# Revit family: ledwall-mounted-p_rd300-15w_543011000600
name_source: partatom
category: Leuchten
revit_build: Autodesk Revit 2016 (Build: 20190508_0715(x64)
units: mm (PartAtom-declared; Revit-internal decimal feet)

## family parameters
Basisbauteil = Fläche
Beim Laden mit Abzugskörper schneiden = Nein
Bemaßung runder Anschluss = Durchmesser verwenden
Gemeinsam genutzt = Nein
Lichtquelle = Nein
Raumberechnungspunkt = Nein
Teiletyp = Normal

## types (1)
- LEDWall-Mounted-P Rd300-15W (1 x LED, 1750 lm)
    Approval mark = CE, ENEC
    Beschreibung = Robust, waterproof IP65 LED luminaire with high degree impact protection (IK10). Well integrated in architecture thanks to its comfortable light distribution. Designed to be easy to install and maintain with up to 2.5mm² through-wiring possibility. Suitable for both indoor and outdoor applications. Energy savings up to 60% compared to compact fluorescent based fixtures.
    CIE Flux Codes = 45 76 94 97 100
    Control Gear = Electronic ballast
    Height = 84 mm
    Hersteller = OPPLE
    Lamp Light Flux = 1750 lm
    Lamp count = 1
    Lampe = 1 x LED
    Length = 322 mm
    Luminous efficacy = 117 lm/W
    ModVariant = Nein
    Modell = 543011000600
    Mounting Place = Wall
    Mounting Type = Surface mounted
    Number of Poles = 1
    OnlyDefault = Ja
    Power Factor = 1
    Product Name = LEDWall-Mounted-P Rd300-15W
    Product group = Wall-Mounted Performer
    ProductGroupID = 2022
    Protection Class = Protection class II
    Protection Degree = IP 65
    RLX_Detail_Level = 1
    RlxData = <blob elided: 44117 chars, md5=4c1a94bc>
    Scheinlast = 15 VA
    Socket = socket
    Standby Power = 0 W
    System Light Flux = 1750 lm
    System Power = 15 W
    Typenbild = 543011000600.jpg
    Typenkommentare = Product without accessories
    URL = http://relux.com
    VarID = ---
    Voltage = 0 V
    Vorgabe-Ansicht = 1800 mm
    Weight = 0.00 kg
    Width = 0 mm  [stored 0 ft]

note: [stored X ft] marks values corroborated as IEEE doubles in the binary element streams (Revit-internal decimal feet)

## geometry (parser evidence)
native form markers: Sweep x13
no freeform markers — native parametric forms only
